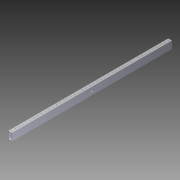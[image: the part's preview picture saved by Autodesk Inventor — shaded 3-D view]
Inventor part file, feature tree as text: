
AUTODESK INVENTOR PART (.ipt)
format: ipt  version: 2014 SP1 (Build 180222100, 222)  size: 798,720 bytes
history: native  units: in
note: dims shown in document units (in); Inventor stores cm internally (conversion verified against a paired STEP export)
features: other x2, extrude x2, sketch x2, imported_body x1
ambient origin geometry x8: Origin, YZ Plane, XZ Plane, XY Plane, X Axis, Y Axis, Z Axis, Center Point
bodies: Body1 (feature_tree)
feature tree (7):
  other  "Cut-Extrude2"
  other  "2x1 Tube1"
  extrude  "Extrusion1"  Depth=0.5in
  extrude  "Extrusion2"  Depth=1.0in TaperAngle=0.0deg
  imported_body  "Base1"
  sketch  "Sketch1"  dims[d0=16.0in d1=0.0in d2=0.5in]
  sketch  "Sketch2"  dims[d3=21.5in d4=1.0in d5=0.0in]
